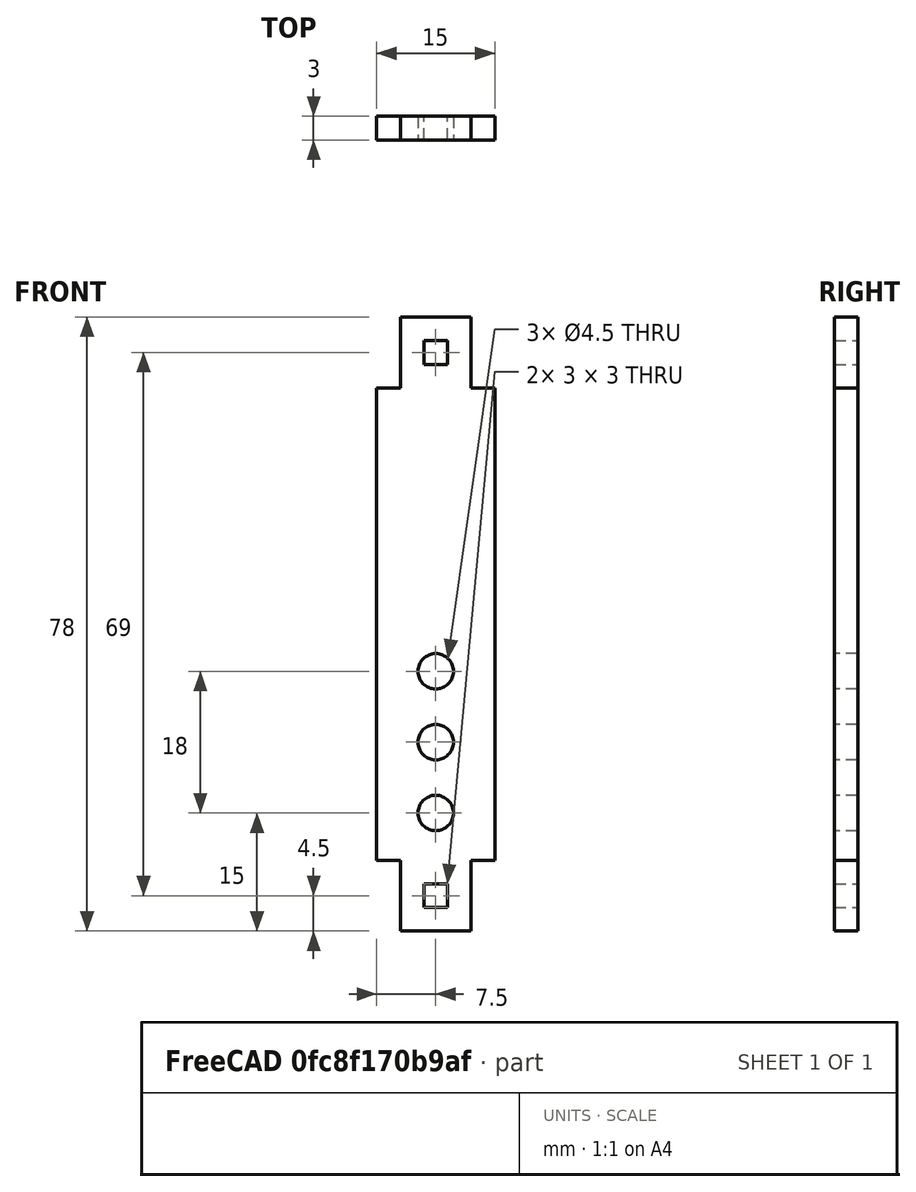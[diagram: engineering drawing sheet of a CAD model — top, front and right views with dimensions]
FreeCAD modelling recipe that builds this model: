
FCSTD DOCUMENT  (FreeCAD 0.16R6707 (Git))
Label: turretPitchRingConnector60
License: All rights reserved
LicenseURL: http://en.wikipedia.org/wiki/All_rights_reserved
objects: Part::Box×5, Part::Cut×5, Part::Cylinder×3, Part::MultiFuse×1
note: 14 computed .brp shape members not serialized (recipe doc carries the construction recipe); baked Part::Feature solids carry a one-line shape summary decoded from their .brp

FEATURE [Part::Box] Box009  label="Cube009"
  Height = 9
  Length = 9
  Placement = pos=(-4.5,-66,3) rot=(0,0,1;0rad)
  Width = 3
FEATURE [Part::Box] Box010  label="Cube010"
  Height = 3
  Length = 3
  Placement = pos=(-1.5,-66,6) rot=(0,0,1;0rad)
  Width = 3
FEATURE [Part::Cut] Cut010
  Base = -> Box009
  Placement = pos=(0,0,30) rot=(0,0,1;0rad)
  Tool = -> Box010
FEATURE [Part::Box] Box011  label="Cube011"
  Height = 60
  Length = 15
  Placement = pos=(-7.5,-66,-27) rot=(0,0,1;0rad)
  Width = 3
FEATURE [Part::Box] Box012  label="Cube012"
  Height = 9
  Length = 9
  Placement = pos=(-4.5,-66,3) rot=(0,0,1;0rad)
  Width = 3
FEATURE [Part::Box] Box013  label="Cube013"
  Height = 3
  Length = 3
  Placement = pos=(-1.5,-66,6) rot=(0,0,1;0rad)
  Width = 3
FEATURE [Part::Cut] Cut011
  Base = -> Box012
  Placement = pos=(0,0,-39) rot=(0,0,1;0rad)
  Tool = -> Box013
FEATURE [Part::MultiFuse] Fusion
  Shapes = -> [Cut011,Box011,Cut010]
FEATURE [Part::Cylinder] Cylinder004
  Angle = 360
  Height = 3
  Placement = pos=(0,-63,-12) rot=(1,0,0;1.5708rad)
  Radius = 2.25
FEATURE [Part::Cylinder] Cylinder005
  Angle = 360
  Height = 3
  Placement = pos=(0,-63,-3) rot=(1,0,0;1.5708rad)
  Radius = 2.25
FEATURE [Part::Cylinder] Cylinder006
  Angle = 360
  Height = 3
  Placement = pos=(0,-63,-21) rot=(1,0,0;1.5708rad)
  Radius = 2.25
FEATURE [Part::Cut] Cut012
  Base = -> Fusion
  Tool = -> Cylinder004
FEATURE [Part::Cut] Cut013
  Base = -> Cut012
  Tool = -> Cylinder006
FEATURE [Part::Cut] Cut014  label="pitchRingConnector"
  Base = -> Cut013
  Placement = pos=(0,29,-3) rot=(0,0,1;0rad)
  Tool = -> Cylinder005
